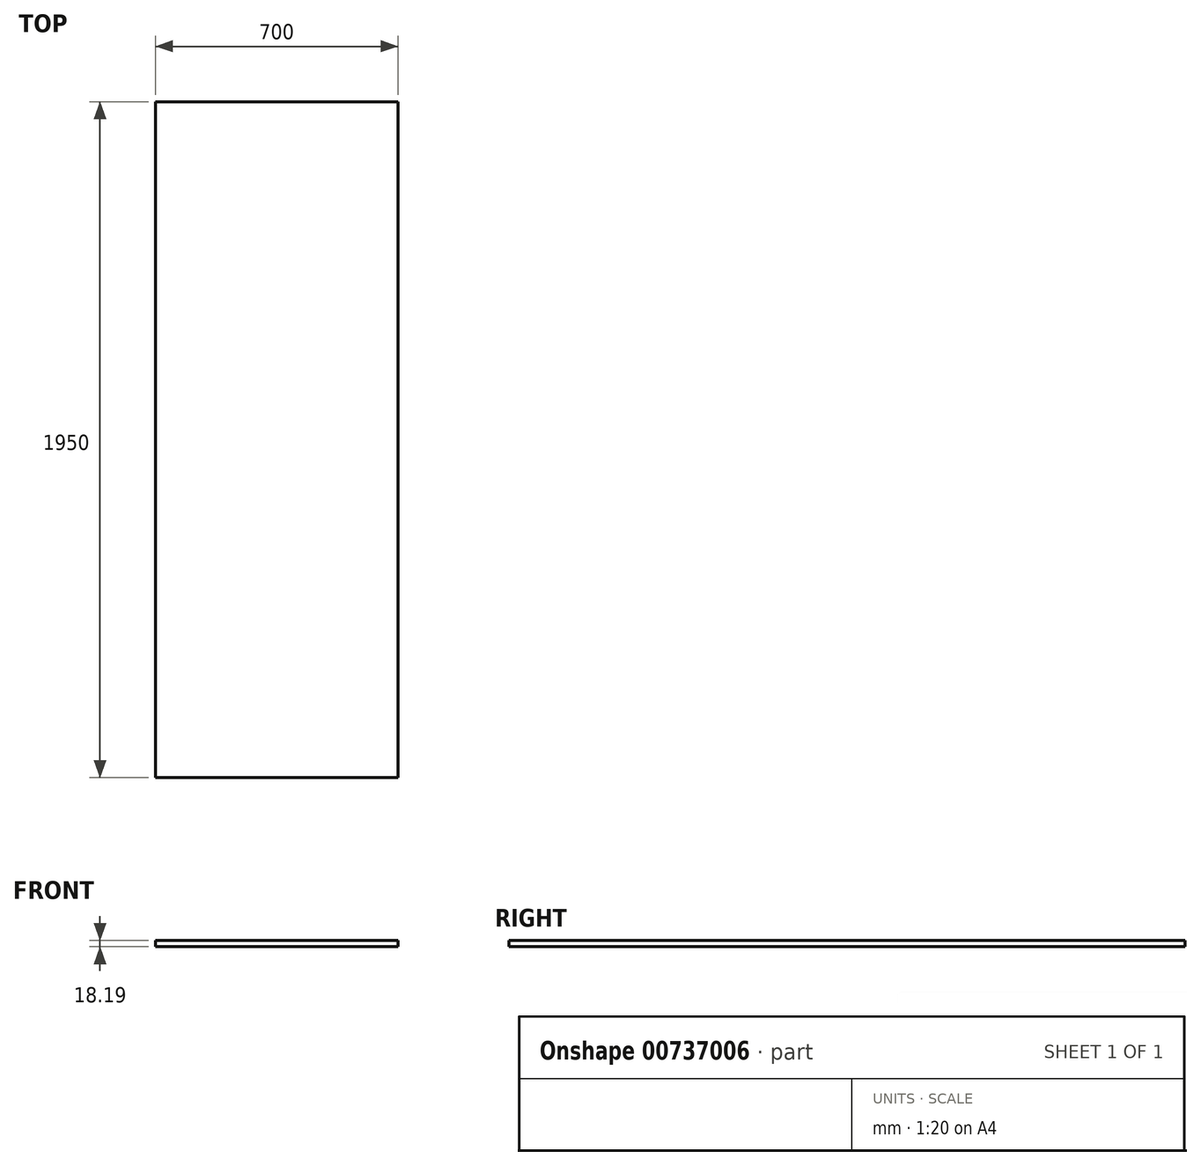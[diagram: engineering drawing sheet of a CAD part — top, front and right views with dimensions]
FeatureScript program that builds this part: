
annotation { "Feature Type Name" : "Feature", "Feature Type Description" : "" }
export const myFeature = defineFeature(function(context is Context, id is Id, definition is map)
    precondition{}
    {
        {
            var Q0;
            Q0=qCreatedBy(makeId("Top.planeOp"),FACE);
            var sketch = newSketch(context, id + "F0", { "sketchPlane" : qUnion([Q0])});
            skLineSegment(sketch, "E0.bottom", {"start": v(-402.74, -910.96) * mm, "end": v(297.26, -910.96) * mm});
            skLineSegment(sketch, "E0.top", {"start": v(-402.74, 1039.04) * mm, "end": v(297.26, 1039.04) * mm});
            skLineSegment(sketch, "E0.left", {"start": v(-402.74, -910.96) * mm, "end": v(-402.74, 1039.04) * mm});
            skLineSegment(sketch, "E0.right", {"start": v(297.26, -910.96) * mm, "end": v(297.26, 1039.04) * mm});
            skSolve(sketch);
        }
        {
            var Q0;
            Q0=makeQuery(id+"F0.imprint","IMPRINT",FACE,{"disambiguationData":[TD([[makeQuery(id+"F0.imprint","IMPRINT",EDGE,{"derivedFrom":sQuery(id+"F0.wireOp",EDGE,"E0.bottom")}),1.0]])]});
            extrude(context, id + "F1", {"entities" : qUnion([Q0]), "depth" : 18.2 * mm, "offsetDistance" : 25 * mm});
        }
    });
